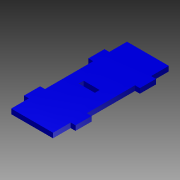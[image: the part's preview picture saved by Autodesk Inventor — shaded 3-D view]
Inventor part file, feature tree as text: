
AUTODESK INVENTOR PART (.ipt)
format: ipt  version: 2012 (Build 160160000, 160)  size: 103,936 bytes
history: native  units: mm
features: extrude x1, sketch x1
ambient origin geometry x8: Origin, YZ Plane, XZ Plane, XY Plane, X Axis, Y Axis, Z Axis, Center Point
bodies: Solid1 (feature_tree)
feature tree (2):
  extrude  "Extrusion1"  Depth=3.0mm
  sketch  "Sketch1"  dims[d19=10.0mm d20=3.0mm d21=32.0mm d22=10.0mm d23=3.0mm d24=30.0mm d25=3.0mm d26=10.0mm d27=32.0mm d28=10.0mm d29=3.0mm d30=3.0mm d31=10.0mm d32=7.5mm d33=3.0mm d34=0.0mm d35=30.0mm d36=72.0mm d39=34.5mm d40=26.0mm d41=26.0mm d42=11.0mm d43=11.0mm]
